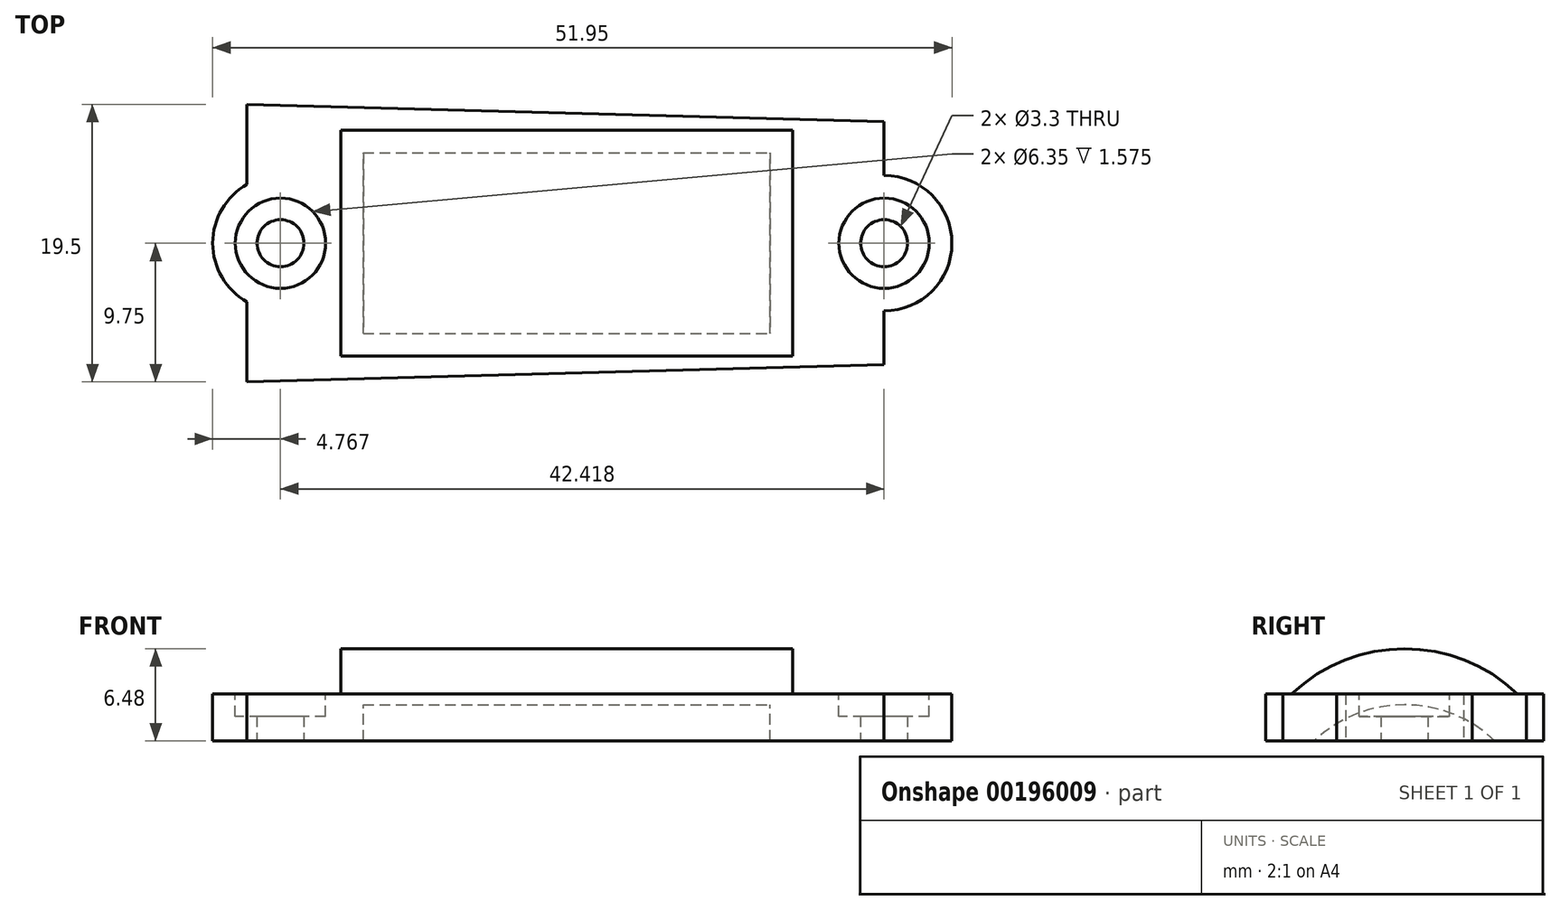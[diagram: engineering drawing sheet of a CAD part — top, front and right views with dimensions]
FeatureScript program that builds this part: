
annotation { "Feature Type Name" : "Feature", "Feature Type Description" : "" }
export const myFeature = defineFeature(function(context is Context, id is Id, definition is map)
    precondition{}
    {
        {
            var Q0;
            Q0=qCreatedBy(makeId("Top.planeOp"),FACE);
            var sketch = newSketch(context, id + "F0", { "sketchPlane" : qUnion([Q0])});
            skLineSegment(sketch, "E0", {"start": v(-22.47, 0) * mm, "end": v(22.32, 0) * mm, "construction": true});
            skLineSegment(sketch, "E1", {"start": v(22.32, 4.76) * mm, "end": v(22.32, 8.55) * mm});
            skLineSegment(sketch, "E2", {"start": v(22.32, 8.55) * mm, "end": v(-22.47, 9.75) * mm});
            skLineSegment(sketch, "E3", {"start": v(-22.47, 9.75) * mm, "end": v(-22.47, 4.14) * mm});
            skLineSegment(sketch, "E4", {"start": v(-22.47, -9.75) * mm, "end": v(22.32, -8.55) * mm});
            skLineSegment(sketch, "E5", {"start": v(22.32, -8.55) * mm, "end": v(22.32, -4.76) * mm});
            skArc(sketch, "E6", {"start": v(22.32, -4.76) * mm, "mid": v(27.08, 0) * mm, "end": v(22.32, 4.76) * mm});
            skArc(sketch, "E7", {"start": v(-22.47, 4.14) * mm, "mid": v(-24.87, 0) * mm, "end": v(-22.47, -4.14) * mm});
            skLineSegment(sketch, "E8.trimOffspring", {"start": v(-22.47, -4.14) * mm, "end": v(-22.47, -9.75) * mm});
            skCircle(sketch, "E9", {"center": v(-20.1, 0) * mm, "radius": 1.65 * mm});
            skCircle(sketch, "E10", {"center": v(22.32, 0) * mm, "radius": 1.65 * mm});
            skSolve(sketch);
        }
        {
            var Q0;
            Q0=makeQuery(id+"F0.imprint","IMPRINT",FACE,{"disambiguationData":[TD([[makeQuery(id+"F0.imprint","IMPRINT",EDGE,{"derivedFrom":sQuery(id+"F0.wireOp",EDGE,"E1")}),1.0]])]});
            extrude(context, id + "F1", {"entities" : qUnion([Q0]), "depth" : 3.3 * mm});
        }
        {
            var Q0;
            Q0=makeQuery(id+"F1.opExtrude","CAP_FACE",FACE,{"disambiguationData":[OSD([sQuery(id+"F0.wireOp",EDGE,"E1"),sQuery(id+"F0.wireOp",EDGE,"E2"),sQuery(id+"F0.wireOp",EDGE,"E3"),sQuery(id+"F0.wireOp",EDGE,"E4"),sQuery(id+"F0.wireOp",EDGE,"E5"),sQuery(id+"F0.wireOp",EDGE,"E6"),sQuery(id+"F0.wireOp",EDGE,"E7"),sQuery(id+"F0.wireOp",EDGE,"E8.trimOffspring"),sQuery(id+"F0.wireOp",EDGE,"E9"),sQuery(id+"F0.wireOp",EDGE,"E10")])],"isStart":false});
            var sketch = newSketch(context, id + "F2", { "sketchPlane" : qUnion([Q0])});
            skCircle(sketch, "E11", {"center": v(-20.1, 0) * mm, "radius": 3.18 * mm});
            skCircle(sketch, "E12", {"center": v(22.32, 0) * mm, "radius": 3.18 * mm});
            skSolve(sketch);
        }
        {
            var Q0;
            Q0=makeQuery(id+"F2.imprint","IMPRINT",FACE,{"disambiguationData":[TD([[makeQuery(id+"F2.imprint","IMPRINT",EDGE,{"derivedFrom":sQuery(id+"F2.wireOp",EDGE,"E11")}),1.0]])]});
            var Q1;
            Q1=makeQuery(id+"F2.imprint","IMPRINT",FACE,{"disambiguationData":[TD([[makeQuery(id+"F2.imprint","IMPRINT",EDGE,{"derivedFrom":sQuery(id+"F2.wireOp",EDGE,"E12")}),1.0]])]});
            extrude(context, id + "F3", {"entities" : qUnion([Q0, Q1]), "operationType" : NewBodyOperationType.REMOVE, "oppositeDirection" : true, "depth" : 1.57 * mm});
        }
        {
            var Q0;
            Q0=qCreatedBy(makeId("Right.planeOp"),FACE);
            var sketch = newSketch(context, id + "F4", { "sketchPlane" : qUnion([Q0])});
            skLineSegment(sketch, "E13", {"start": v(-7.94, 3.3) * mm, "end": v(7.94, 3.3) * mm});
            skArc(sketch, "E14", {"start": v(7.94, 3.3) * mm, "mid": v(0, 6.48) * mm, "end": v(-7.94, 3.3) * mm});
            skLineSegment(sketch, "E15", {"start": v(0, 0) * mm, "end": v(0, 3.3) * mm, "construction": true});
            skSolve(sketch);
        }
        {
            var Q0;
            Q0=makeQuery(id+"F4.imprint","IMPRINT",FACE,{"disambiguationData":[TD([[makeQuery(id+"F4.imprint","IMPRINT",EDGE,{"derivedFrom":sQuery(id+"F4.wireOp",EDGE,"E13")}),1.0]])]});
            extrude(context, id + "F5", {"entities" : qUnion([Q0]), "operationType" : NewBodyOperationType.ADD, "endBound" : BoundingType.SYMMETRIC, "depth" : 31.75 * mm});
        }
        {
            var Q0;
            Q0=qCreatedBy(makeId("Right.planeOp"),FACE);
            var sketch = newSketch(context, id + "F6", { "sketchPlane" : qUnion([Q0])});
            skLineSegment(sketch, "E16", {"start": v(-6.35, 0) * mm, "end": v(6.35, 0) * mm});
            skArc(sketch, "E17", {"start": v(6.35, 0) * mm, "mid": v(0, 2.54) * mm, "end": v(-6.35, 0) * mm});
            skSolve(sketch);
        }
        {
            var Q0;
            Q0 = qSketchRegion(id + "F6", true);
            extrude(context, id + "F7", {"entities" : qUnion([Q0]), "operationType" : NewBodyOperationType.REMOVE, "endBound" : BoundingType.SYMMETRIC, "oppositeDirection" : true, "depth" : 28.57 * mm});
        }
    });
